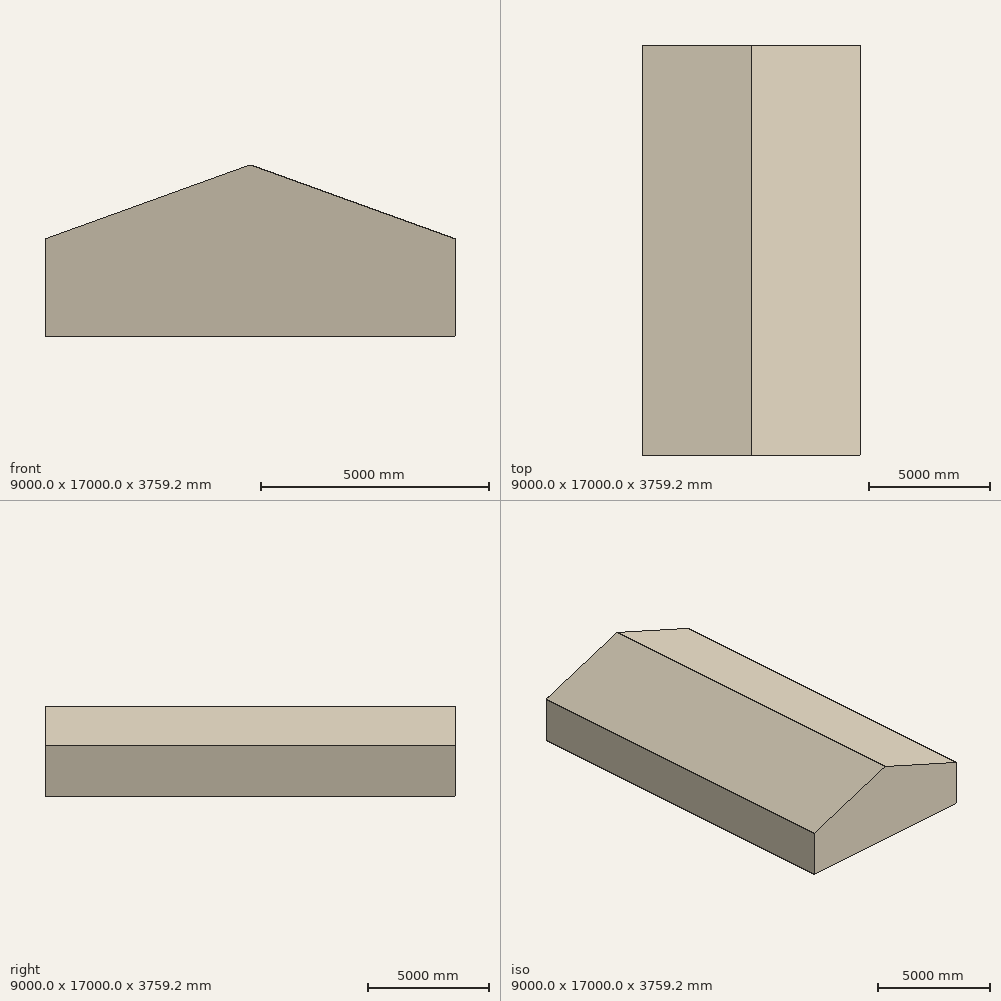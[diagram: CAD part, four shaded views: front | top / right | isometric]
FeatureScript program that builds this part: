
annotation { "Feature Type Name" : "Feature", "Feature Type Description" : "" }
export const myFeature = defineFeature(function(context is Context, id is Id, definition is map)
    precondition{}
    {
        {
            var Q0;
            Q0=qCreatedBy(makeId("Top.planeOp"),FACE);
            var sketch = newSketch(context, id + "F0", { "sketchPlane" : qUnion([Q0])});
            skLineSegment(sketch, "E0.bottom", {"start": v(0, 0) * mm, "end": v(-9000, 0) * mm});
            skLineSegment(sketch, "E0.top", {"start": v(0, 17000) * mm, "end": v(-9000, 17000) * mm});
            skLineSegment(sketch, "E0.left", {"start": v(0, 0) * mm, "end": v(0, 17000) * mm});
            skLineSegment(sketch, "E0.right", {"start": v(-9000, 0) * mm, "end": v(-9000, 17000) * mm});
            skSolve(sketch);
        }
        {
            var Q0;
            Q0=makeQuery(id+"F0.imprint","IMPRINT",FACE,{"disambiguationData":[TD([[makeQuery(id+"F0.imprint","IMPRINT",EDGE,{"derivedFrom":sQuery(id+"F0.wireOp",EDGE,"E0.bottom")}),-1.0]])]});
            extrude(context, id + "F1", {"entities" : qUnion([Q0]), "depth" : 3759.2 * mm, "offsetDistance" : 25 * mm});
        }
        {
            var Q0;
            Q0=makeQuery(id+"F1.opExtrude","SWEPT_FACE",FACE,{"disambiguationData":[OSD([sQuery(id+"F0.wireOp",EDGE,"E0.bottom")])]});
            var sketch = newSketch(context, id + "F2", { "sketchPlane" : qUnion([Q0])});
            skLineSegment(sketch, "E1", {"start": v(0, 0) * mm, "end": v(0, 2133.6) * mm});
            skLineSegment(sketch, "E2", {"start": v(0, 2133.6) * mm, "end": v(-4500, 3759.2) * mm});
            skLineSegment(sketch, "E3", {"start": v(-9000, 0) * mm, "end": v(-9000, 2133.6) * mm});
            skLineSegment(sketch, "E4", {"start": v(-9000, 2133.6) * mm, "end": v(-4500, 3759.2) * mm});
            skLineSegment(sketch, "E5", {"start": v(-9000, 0) * mm, "end": v(-8900, 0) * mm});
            skLineSegment(sketch, "E6", {"start": v(-4500, 3759.2) * mm, "end": v(-4500, 3659.2) * mm});
            skLineSegment(sketch, "E7", {"start": v(-4500, 3659.2) * mm, "end": v(-8923.94, 2061.08) * mm});
            skLineSegment(sketch, "E8", {"start": v(-8900, 0) * mm, "end": v(-8900, 2069.72) * mm});
            skLineSegment(sketch, "E9", {"start": v(0, 0) * mm, "end": v(-100, 0) * mm});
            skLineSegment(sketch, "E10", {"start": v(-100, 0) * mm, "end": v(-100, 2118.38) * mm});
            skLineSegment(sketch, "E11", {"start": v(-4500, 3659.2) * mm, "end": v(-100, 2069.72) * mm});
            skSolve(sketch);
        }
        {
            var Q0;
            {var subQ0=sQuery(id+"F2.wireOp",EDGE,"E4");Q0=makeQuery(id+"F2.imprint","IMPRINT",FACE,{"disambiguationData":[TD([[makeQuery(id+"F2.imprint","IMPRINT",EDGE,{"derivedFrom":subQ0}),1.0]])]});}
            var Q1;
            {var subQ0=sQuery(id+"F2.wireOp",EDGE,"E2");Q1=makeQuery(id+"F2.imprint","IMPRINT",FACE,{"disambiguationData":[TD([[makeQuery(id+"F2.imprint","IMPRINT",EDGE,{"derivedFrom":subQ0}),-1.0]])]});}
            extrude(context, id + "F3", {"entities" : qUnion([Q0, Q1]), "operationType" : NewBodyOperationType.REMOVE, "oppositeDirection" : true, "depth" : 17000 * mm, "offsetDistance" : 25 * mm});
        }
        {
            var Q0;
            {var subQ4=sQuery(id+"F2.wireOp",EDGE,"E8");Q0=makeQuery(id+"F2.imprint","IMPRINT",FACE,{"disambiguationData":[TD([[makeQuery(id+"F2.imprint","IMPRINT",EDGE,{"derivedFrom":subQ4}),-1.0]])]});}
            extrude(context, id + "F4", {"entities" : qUnion([Q0]), "operationType" : NewBodyOperationType.REMOVE, "oppositeDirection" : true, "depth" : 16900 * mm, "offsetDistance" : 25 * mm});
        }
        {
            var Q0;
            {var subQ4=sQuery(id+"F2.wireOp",EDGE,"E8");Q0=makeQuery(id+"F2.imprint","IMPRINT",FACE,{"disambiguationData":[TD([[makeQuery(id+"F2.imprint","IMPRINT",EDGE,{"derivedFrom":subQ4}),-1.0]])]});}
            extrude(context, id + "F5", {"entities" : qUnion([Q0]), "operationType" : NewBodyOperationType.ADD, "oppositeDirection" : true, "depth" : 100 * mm, "offsetDistance" : 25 * mm});
        }
    });
